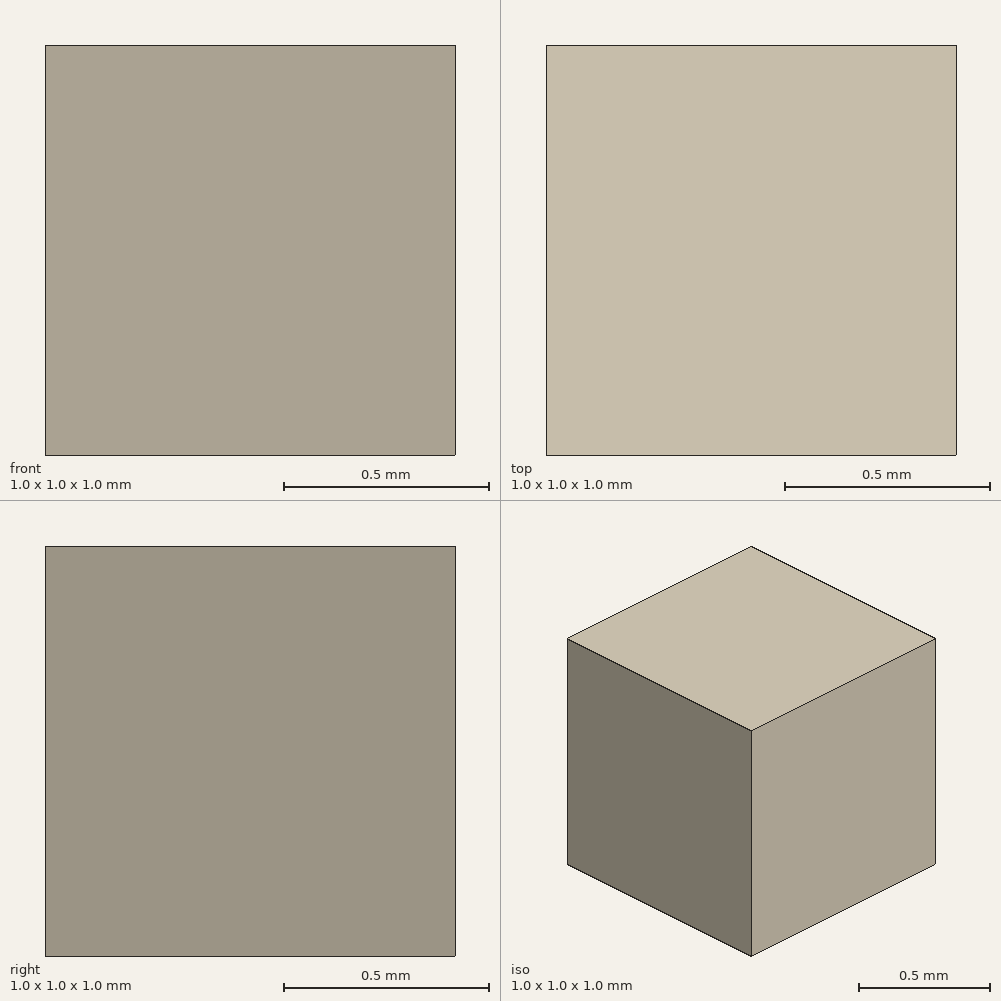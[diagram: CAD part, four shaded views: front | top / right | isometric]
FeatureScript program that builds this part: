
annotation { "Feature Type Name" : "Feature", "Feature Type Description" : "" }
export const myFeature = defineFeature(function(context is Context, id is Id, definition is map)
    precondition{}
    {
        {
            var Q0;
            Q0=qCreatedBy(makeId("Top.planeOp"),FACE);
            var sketch = newSketch(context, id + "F0", { "sketchPlane" : qUnion([Q0])});
            skLineSegment(sketch, "E0.bottom", {"start": v(0, 0) * mm, "end": v(1, 0) * mm});
            skLineSegment(sketch, "E0.top", {"start": v(0, 1) * mm, "end": v(1, 1) * mm});
            skLineSegment(sketch, "E0.left", {"start": v(0, 0) * mm, "end": v(0, 1) * mm});
            skLineSegment(sketch, "E0.right", {"start": v(1, 0) * mm, "end": v(1, 1) * mm});
            skSolve(sketch);
        }
        {
            var Q0;
            Q0=makeQuery(id+"F0.imprint","IMPRINT",FACE,{"disambiguationData":[TD([[makeQuery(id+"F0.imprint","IMPRINT",EDGE,{"derivedFrom":sQuery(id+"F0.wireOp",EDGE,"E0.bottom")}),1.0]])]});
            extrude(context, id + "F1", {"entities" : qUnion([Q0]), "depth" : 1 * mm});
        }
    });
